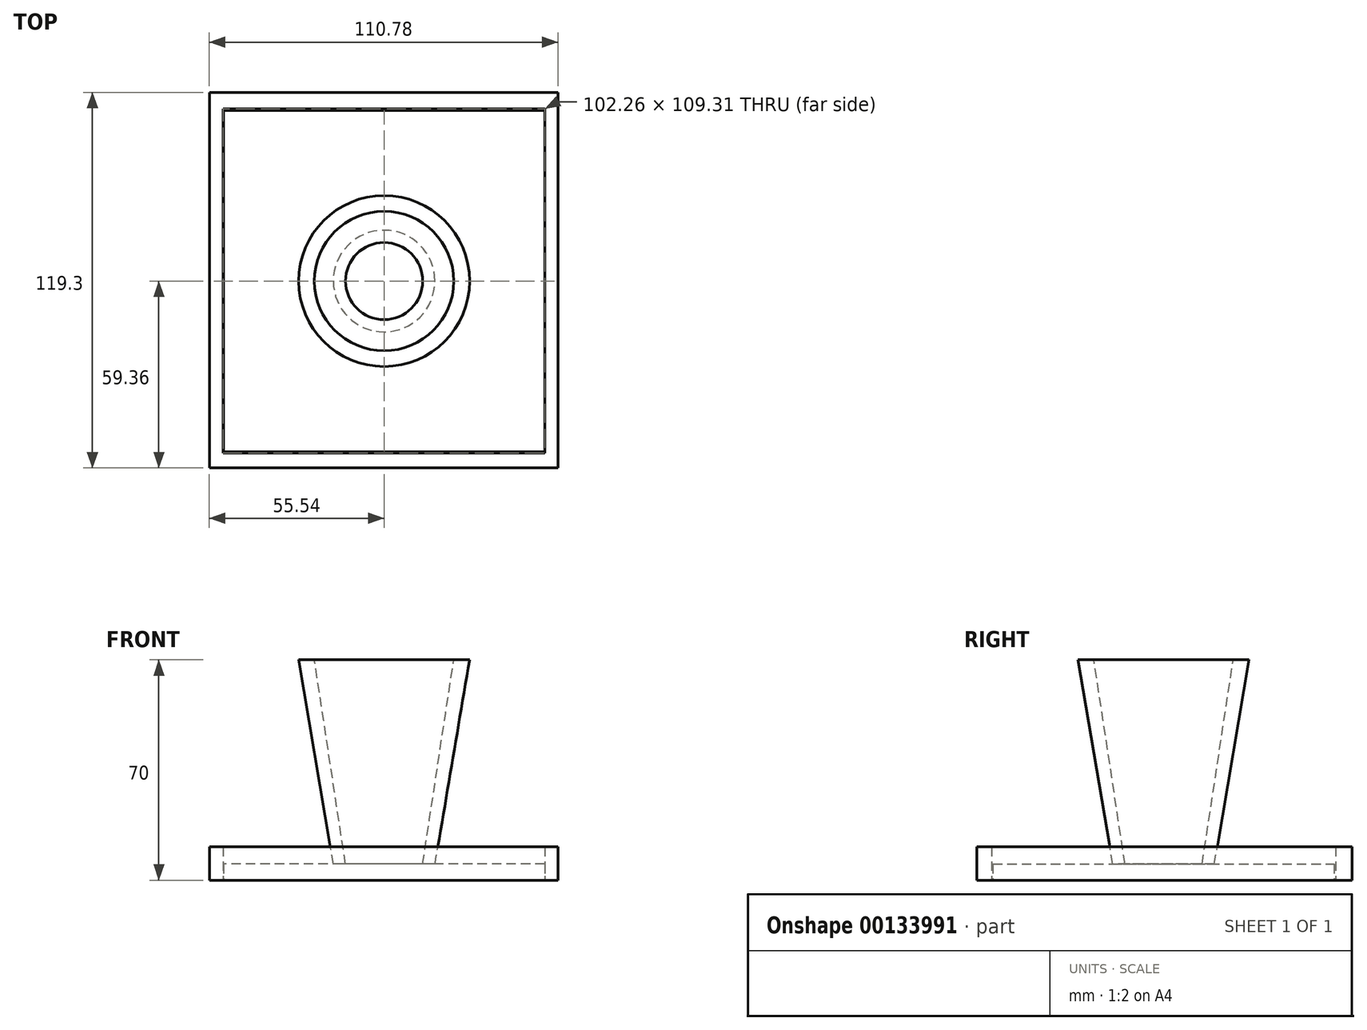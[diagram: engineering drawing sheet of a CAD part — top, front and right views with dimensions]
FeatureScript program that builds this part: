
annotation { "Feature Type Name" : "Feature", "Feature Type Description" : "" }
export const myFeature = defineFeature(function(context is Context, id is Id, definition is map)
    precondition{}
    {
        {
            var Q0;
            Q0=qCreatedBy(makeId("Top.planeOp"),FACE);
            var sketch = newSketch(context, id + "F0", { "sketchPlane" : qUnion([Q0])});
            skLineSegment(sketch, "E0.bottom", {"start": v(-51.13, 54.65) * mm, "end": v(51.13, 54.65) * mm});
            skLineSegment(sketch, "E0.top", {"start": v(-51.13, -54.65) * mm, "end": v(51.13, -54.65) * mm});
            skLineSegment(sketch, "E0.left", {"start": v(-51.13, 54.65) * mm, "end": v(-51.13, -54.65) * mm});
            skLineSegment(sketch, "E0.right", {"start": v(51.13, 54.65) * mm, "end": v(51.13, -54.65) * mm});
            skPoint(sketch, "E0.middle", {"position": v(0, 0) * mm});
            skLineSegment(sketch, "E1.bottom", {"start": v(-51.13, 54.65) * mm, "end": v(-55.54, 54.65) * mm});
            skLineSegment(sketch, "E1.top", {"start": v(-51.13, -54.65) * mm, "end": v(-55.54, -54.65) * mm});
            skLineSegment(sketch, "E1.right", {"start": v(-55.54, 54.65) * mm, "end": v(-55.54, -54.65) * mm});
            skLineSegment(sketch, "E2.bottom", {"start": v(-55.54, -54.65) * mm, "end": v(51.13, -54.65) * mm});
            skLineSegment(sketch, "E2.top", {"start": v(-55.54, -59.36) * mm, "end": v(51.13, -59.36) * mm});
            skLineSegment(sketch, "E2.left", {"start": v(-55.54, -54.65) * mm, "end": v(-55.54, -59.36) * mm});
            skLineSegment(sketch, "E2.right", {"start": v(51.13, -54.65) * mm, "end": v(51.13, -59.36) * mm});
            skLineSegment(sketch, "E3.bottom", {"start": v(51.13, -59.36) * mm, "end": v(55.24, -59.36) * mm});
            skLineSegment(sketch, "E3.top", {"start": v(51.13, 59.94) * mm, "end": v(55.24, 59.94) * mm});
            skLineSegment(sketch, "E3.left", {"start": v(51.13, -59.36) * mm, "end": v(51.13, 59.94) * mm});
            skLineSegment(sketch, "E3.right", {"start": v(55.24, -59.36) * mm, "end": v(55.24, 59.94) * mm});
            skLineSegment(sketch, "E4.bottom", {"start": v(55.24, 59.94) * mm, "end": v(-55.54, 59.94) * mm});
            skLineSegment(sketch, "E4.top", {"start": v(55.24, 54.65) * mm, "end": v(-55.54, 54.65) * mm});
            skLineSegment(sketch, "E4.left", {"start": v(55.24, 59.94) * mm, "end": v(55.24, 54.65) * mm});
            skLineSegment(sketch, "E4.right", {"start": v(-55.54, 59.94) * mm, "end": v(-55.54, 54.65) * mm});
            skCircle(sketch, "E5", {"center": v(0, 0) * mm, "radius": 15.28 * mm});
            skCircle(sketch, "E6", {"center": v(0, 0) * mm, "radius": 18.5 * mm});
            skSolve(sketch);
        }
        {
            var Q0;
            Q0=qCreatedBy(makeId("Top.planeOp"),FACE);
            cPlane(context, id + "F1", {"entities" : qUnion([Q0]), "cplaneType" : CPlaneType.OFFSET, "offset" : 70 * mm, "width" : 150 * mm, "height" : 150 * mm});
        }
        {
            var Q0;
            Q0=qCreatedBy(id+"F1.planeOp",FACE);
            var sketch = newSketch(context, id + "F2", { "sketchPlane" : qUnion([Q0])});
            skCircle(sketch, "E7", {"center": v(0, 0) * mm, "radius": 27.16 * mm});
            skCircle(sketch, "E8", {"center": v(0, 0) * mm, "radius": 31.16 * mm});
            skSolve(sketch);
        }
        {
            var Q0;
            Q0=makeQuery(id+"F2.imprint","IMPRINT",FACE,{"disambiguationData":[TD([[makeQuery(id+"F2.imprint","IMPRINT",EDGE,{"derivedFrom":sQuery(id+"F2.wireOp",EDGE,"E7")}),1.0]])]});
            var Q1;
            Q1=makeQuery(id+"F0.imprint","IMPRINT",FACE,{"disambiguationData":[TD([[makeQuery(id+"F0.imprint","IMPRINT",EDGE,{"derivedFrom":sQuery(id+"F0.wireOp",EDGE,"E5")}),1.0]])]});
            loft(context, id + "F3", {"sheetProfilesArray" : [{ "sheetProfileEntities" : qUnion([Q0]) }, { "sheetProfileEntities" : qUnion([Q1]) }]});
        }
        {
            var Q0;
            Q0 = qSketchRegion(id + "F0", true);
            extrude(context, id + "F4", {"entities" : qUnion([Q0]), "depth" : 10.57 * mm});
        }
        {
            var Q0;
            Q0=makeQuery(id+"F3.opLoft","CAP_FACE",FACE,{"disambiguationData":[OSD([makeQuery(id+"F2.imprint","IMPRINT",FACE,{"disambiguationData":[TD([[makeQuery(id+"F2.imprint","IMPRINT",EDGE,{"derivedFrom":sQuery(id+"F2.wireOp",EDGE,"E7")}),1.0]])]})])],"isStart":true});
            var sketch = newSketch(context, id + "F5", { "sketchPlane" : qUnion([Q0])});
            skCircle(sketch, "E9", {"center": v(0, 0) * mm, "radius": 22.14 * mm});
            skSolve(sketch);
        }
        {
            var Q0;
            Q0=qCreatedBy(makeId("Top.planeOp"),FACE);
            var sketch = newSketch(context, id + "F6", { "sketchPlane" : qUnion([Q0])});
            skCircle(sketch, "E10", {"center": v(0, 0) * mm, "radius": 11.47 * mm});
            skSolve(sketch);
        }
        {
            var Q1;
            Q1=makeQuery(id+"F5.imprint","IMPRINT",FACE,{"disambiguationData":[TD([[makeQuery(id+"F5.imprint","IMPRINT",EDGE,{"derivedFrom":sQuery(id+"F5.wireOp",EDGE,"E9")}),1.0]])]});
            var Q2;
            Q2=makeQuery(id+"F6.imprint","IMPRINT",FACE,{"disambiguationData":[TD([[makeQuery(id+"F6.imprint","IMPRINT",EDGE,{"derivedFrom":sQuery(id+"F6.wireOp",EDGE,"E10")}),1.0]])]});
            loft(context, id + "F7", {"operationType" : NewBodyOperationType.REMOVE, "sheetProfilesArray" : [{ "sheetProfileEntities" : qUnion([Q1]) }, { "sheetProfileEntities" : qUnion([Q2]) }]});
        }
        {
            var Q0;
            Q0=qCreatedBy(makeId("Top.planeOp"),FACE);
            var sketch = newSketch(context, id + "F8", { "sketchPlane" : qUnion([Q0])});
            skLineSegment(sketch, "E11.bottom", {"start": v(51.07, -54.24) * mm, "end": v(-51.07, -54.24) * mm});
            skLineSegment(sketch, "E11.top", {"start": v(51.07, 54.24) * mm, "end": v(-51.07, 54.24) * mm});
            skLineSegment(sketch, "E11.left", {"start": v(51.07, -54.24) * mm, "end": v(51.07, 54.24) * mm});
            skLineSegment(sketch, "E11.right", {"start": v(-51.07, -54.24) * mm, "end": v(-51.07, 54.24) * mm});
            skPoint(sketch, "E11.middle", {"position": v(0, 0) * mm});
            skSolve(sketch);
        }
        {
            var Q0;
            Q0 = qSketchRegion(id + "F8", true);
            extrude(context, id + "F9", {"entities" : qUnion([Q0]), "operationType" : NewBodyOperationType.ADD, "depth" : 5.13 * mm});
        }
        {
            var Q0;
            {var subQ0=sQuery(id+"F8.wireOp",EDGE,"E11.top");var subQ1=sQuery(id+"F8.wireOp",EDGE,"E11.left");var subQ2=sQuery(id+"F8.wireOp",EDGE,"E11.bottom");var subQ3=sQuery(id+"F8.wireOp",EDGE,"E11.right");Q0=makeQuery(id+"F9.boolean.opBoolean","SPLIT",FACE,{"disambiguationData":[TD([makeQuery(id+"F9.opExtrude","SWEPT_FACE",FACE,{"disambiguationData":[OSD([subQ2])]})])],"derivedFrom":makeQuery(id+"F9.opExtrude","CAP_FACE",FACE,{"disambiguationData":[OSD([subQ2,subQ0,subQ1,subQ3])],"isStart":false})});}
            cPlane(context, id + "F10", {"entities" : qUnion([Q0]), "cplaneType" : CPlaneType.OFFSET, "offset" : 50 * mm, "width" : 150 * mm, "height" : 150 * mm});
        }
    });
